# Revit family: DuraCare-Dining_Chair-Perry-
name_source: partatom
category: Furniture
revit_build: Autodesk Revit 2016 (Build: 20150220_1215(x64)
units: mm (PartAtom-declared; Revit-internal decimal feet)

## family parameters
Always vertical = Yes
Cut with Voids When Loaded = No
OmniClass Number = 23.40.20.00
OmniClass Title = General Furniture and Specialties
Room Calculation Point = No
Shared = No
Work Plane-Based = No

## types (2) — shared parameters
Arm Height = 26"
Assembly Code = E2020200
Back Contrasting Finish = DUR - Fabric 2
Boot Finish = DUR - Plastic Boot
Depth = 22 1/2"
Description = Dining Chair 22.5"W x 22.5"D x 33.5"H - aluminum frame - wood grain finish
Height = 33 1/2"
Keynote = 12500
Low Emitting Finish = Yes
Low Emitting Material = Yes
Manufacturer = DuraCare Seating
Product Documentation Link = https://duracareseating.com
Revit Model Built By = https://servex-us.com
Salvage or Reuse = Yes
Seat Height = 19 1/2"
Type Comments = Perry
URL = https://duracareseating.com
Wheel Finish = DUR - Plastic Black
Width = 22 1/2"
zero-valued in all types: Percentage of Recycled Content

## per-type parameters (varying)
| type | LD |
| AC-772 | No |
| AC-772-LD | Yes |

note: column(s) folded — value = type name in every type: Model

## geometry (parser evidence)
native form markers: Sweep x4
no freeform markers — native parametric forms only
